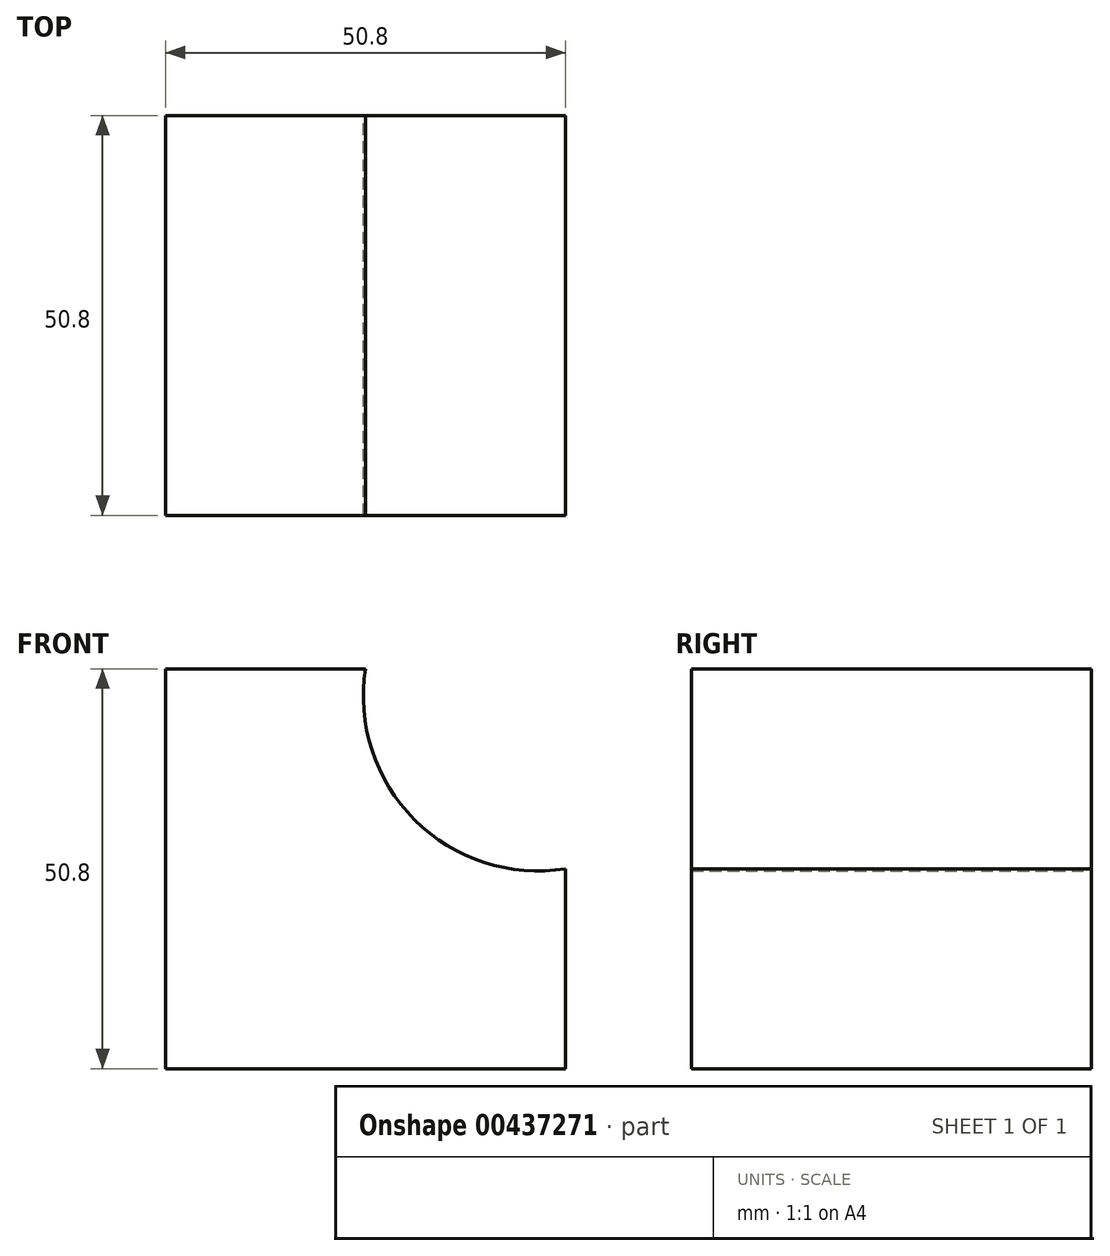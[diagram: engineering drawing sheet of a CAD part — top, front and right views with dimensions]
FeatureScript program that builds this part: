
annotation { "Feature Type Name" : "Feature", "Feature Type Description" : "" }
export const myFeature = defineFeature(function(context is Context, id is Id, definition is map)
    precondition{}
    {
        {
            var Q0;
            Q0=qCreatedBy(makeId("Front.planeOp"),FACE);
            var sketch = newSketch(context, id + "F0", { "sketchPlane" : qUnion([Q0])});
            skLineSegment(sketch, "E0", {"start": v(2.52, 0) * mm, "end": v(53.32, 0) * mm});
            skLineSegment(sketch, "E1", {"start": v(53.32, 0) * mm, "end": v(53.32, 25.4) * mm});
            skLineSegment(sketch, "E2", {"start": v(2.52, 0) * mm, "end": v(2.52, 50.8) * mm});
            skLineSegment(sketch, "E3", {"start": v(2.52, 50.8) * mm, "end": v(27.92, 50.8) * mm});
            skArc(sketch, "E4", {"start": v(27.92, 50.8) * mm, "mid": v(34.14, 31.62) * mm, "end": v(53.32, 25.4) * mm});
            skSolve(sketch);
        }
        {
            var Q0;
            Q0 = qSketchRegion(id + "F0", true);
            extrude(context, id + "F1", {"entities" : qUnion([Q0]), "depth" : 50.8 * mm});
        }
    });
